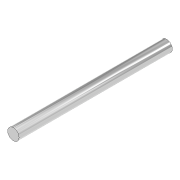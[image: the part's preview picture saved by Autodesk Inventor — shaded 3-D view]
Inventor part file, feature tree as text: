
AUTODESK INVENTOR PART (.ipt)
format: ipt  version: 2020 (Build 240168000, 168)  size: 78,848 bytes
history: native  units: in
note: dims shown in document units (in); Inventor stores cm internally (conversion verified against a paired STEP export)
features: extrude x1, sketch x1
ambient origin geometry x8: Origin, YZ Plane, XZ Plane, XY Plane, X Axis, Y Axis, Z Axis, Center Point
bodies: Solid1 (feature_tree)
feature tree (2):
  extrude  "Extrusion1"  Depth=2.6496in TaperAngle=0.0deg
  sketch  "Sketch1"  dims[d0=0.1969in d1=2.6496in d2=0.0in]
